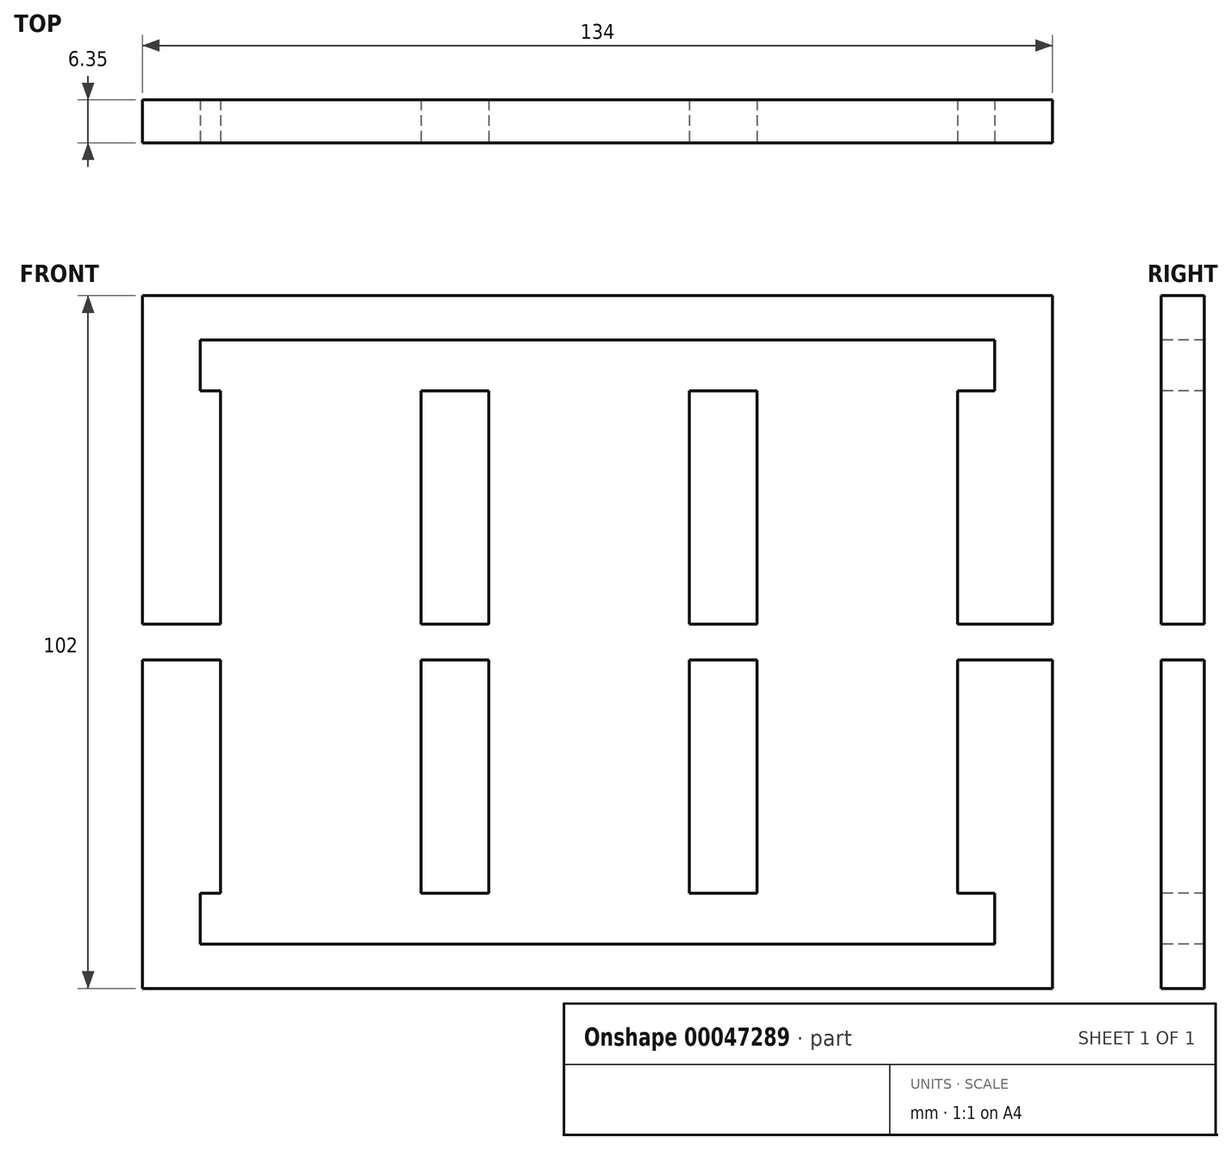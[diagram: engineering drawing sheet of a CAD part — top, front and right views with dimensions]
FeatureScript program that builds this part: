
annotation { "Feature Type Name" : "Feature", "Feature Type Description" : "" }
export const myFeature = defineFeature(function(context is Context, id is Id, definition is map)
    precondition{}
    {
        {
            var Q0;
            Q0=qCreatedBy(makeId("Front.planeOp"),FACE);
            var sketch = newSketch(context, id + "F0", { "sketchPlane" : qUnion([Q0])});
            skLineSegment(sketch, "E0.rect.bottom", {"start": v(67, -51) * mm, "end": v(-67, -51) * mm});
            skLineSegment(sketch, "E0.rect.top", {"start": v(67, 51) * mm, "end": v(-67, 51) * mm});
            skLineSegment(sketch, "E0.rect.left", {"start": v(67, -51) * mm, "end": v(67, 51) * mm});
            skLineSegment(sketch, "E0.rect.right", {"start": v(-67, -51) * mm, "end": v(-67, 51) * mm});
            skPoint(sketch, "E0.rect.middle", {"position": v(0, 0) * mm});
            skLineSegment(sketch, "E1", {"start": v(0, 51) * mm, "end": v(0, -51) * mm, "construction": true});
            skLineSegment(sketch, "E2", {"start": v(-67, 0) * mm, "end": v(67, 0) * mm, "construction": true});
            skSolve(sketch);
        }
        {
            var Q0;
            Q0=makeQuery(id+"F0.imprint","IMPRINT",FACE,{"disambiguationData":[TD([[makeQuery(id+"F0.imprint","IMPRINT",EDGE,{"derivedFrom":sQuery(id+"F0.wireOp",EDGE,"E0.rect.bottom")}),-1.0]])]});
            extrude(context, id + "F1", {"entities" : qUnion([Q0]), "depth" : 6.35 * mm});
        }
        {
            var Q0;
            Q0=makeQuery(id+"F1.opExtrude","CAP_FACE",FACE,{"disambiguationData":[OSD([sQuery(id+"F0.wireOp",EDGE,"E0.rect.bottom"),sQuery(id+"F0.wireOp",EDGE,"E0.rect.top"),sQuery(id+"F0.wireOp",EDGE,"E0.rect.left"),sQuery(id+"F0.wireOp",EDGE,"E0.rect.right")])],"isStart":false});
            var sketch = newSketch(context, id + "F2", { "sketchPlane" : qUnion([Q0])});
            skLineSegment(sketch, "E3.bottom", {"start": v(-16, 39.8) * mm, "end": v(13.5, 39.8) * mm});
            skLineSegment(sketch, "E3.top", {"start": v(-16, -39.8) * mm, "end": v(13.5, -39.8) * mm});
            skLineSegment(sketch, "E3.left", {"start": v(-16, 39.8) * mm, "end": v(-16, -39.8) * mm});
            skLineSegment(sketch, "E3.right", {"start": v(13.5, 39.8) * mm, "end": v(13.5, -39.8) * mm});
            skLineSegment(sketch, "E4.bottom", {"start": v(23.5, 39.8) * mm, "end": v(53, 39.8) * mm});
            skLineSegment(sketch, "E4.top", {"start": v(23.5, -39.8) * mm, "end": v(53, -39.8) * mm});
            skLineSegment(sketch, "E4.left", {"start": v(23.5, 39.8) * mm, "end": v(23.5, -39.8) * mm});
            skLineSegment(sketch, "E4.right", {"start": v(53, 39.8) * mm, "end": v(53, -39.8) * mm});
            skLineSegment(sketch, "E5.bottom", {"start": v(-55.5, 39.8) * mm, "end": v(-26, 39.8) * mm});
            skLineSegment(sketch, "E5.top", {"start": v(-55.5, -39.8) * mm, "end": v(-26, -39.8) * mm});
            skLineSegment(sketch, "E5.left", {"start": v(-55.5, 39.8) * mm, "end": v(-55.5, -39.8) * mm});
            skLineSegment(sketch, "E5.right", {"start": v(-26, 39.8) * mm, "end": v(-26, -39.8) * mm});
            skLineSegment(sketch, "E6", {"start": v(-67, 0) * mm, "end": v(-55.5, 0) * mm, "construction": true});
            skLineSegment(sketch, "E7", {"start": v(53, -16.02) * mm, "end": v(67, -16.02) * mm});
            skSolve(sketch);
        }
        {
            var Q0;
            Q0=qSketchRegion(id+"F2",true);
            extrude(context, id + "F3", {"entities" : qUnion([Q0]), "operationType" : NewBodyOperationType.REMOVE, "oppositeDirection" : true, "depth" : 12.7 * mm});
        }
        {
            var Q0;
            Q0=makeQuery(id+"F1.opExtrude","CAP_FACE",FACE,{"disambiguationData":[OSD([sQuery(id+"F0.wireOp",EDGE,"E0.rect.bottom"),sQuery(id+"F0.wireOp",EDGE,"E0.rect.top"),sQuery(id+"F0.wireOp",EDGE,"E0.rect.left"),sQuery(id+"F0.wireOp",EDGE,"E0.rect.right")])],"isStart":false});
            var sketch = newSketch(context, id + "F4", { "sketchPlane" : qUnion([Q0])});
            skLineSegment(sketch, "E8.bottom", {"start": v(-58.5, 44.5) * mm, "end": v(58.5, 44.5) * mm});
            skLineSegment(sketch, "E8.top", {"start": v(-58.5, 37) * mm, "end": v(58.5, 37) * mm});
            skLineSegment(sketch, "E8.left", {"start": v(-58.5, 44.5) * mm, "end": v(-58.5, 37) * mm});
            skLineSegment(sketch, "E8.right", {"start": v(58.5, 44.5) * mm, "end": v(58.5, 37) * mm});
            skPoint(sketch, "E9.rect.middle", {"position": v(0, 0) * mm});
            skLineSegment(sketch, "E10.rect.bottom", {"start": v(67, -2.63) * mm, "end": v(-67, -2.63) * mm});
            skLineSegment(sketch, "E10.rect.top", {"start": v(67, 2.62) * mm, "end": v(-67, 2.62) * mm});
            skLineSegment(sketch, "E10.rect.left", {"start": v(67, -2.63) * mm, "end": v(67, 2.62) * mm});
            skLineSegment(sketch, "E10.rect.right", {"start": v(-67, -2.63) * mm, "end": v(-67, 2.62) * mm});
            skPoint(sketch, "E11", {"position": v(-67, 0) * mm});
            skPoint(sketch, "E12", {"position": v(67, 0) * mm});
            skLineSegment(sketch, "E13", {"start": v(-67, 0) * mm, "end": v(67, 0) * mm, "construction": true});
            skLineSegment(sketch, "E14.MirrorCS", {"start": v(-58.5, -44.5) * mm, "end": v(-58.5, -37) * mm});
            skLineSegment(sketch, "E15.MirrorCS", {"start": v(-58.5, -44.5) * mm, "end": v(58.5, -44.5) * mm});
            skLineSegment(sketch, "E16.MirrorCS", {"start": v(58.5, -44.5) * mm, "end": v(58.5, -37) * mm});
            skLineSegment(sketch, "E17.MirrorCS", {"start": v(-58.5, -37) * mm, "end": v(58.5, -37) * mm});
            skLineSegment(sketch, "E18", {"start": v(-58.5, 37) * mm, "end": v(-67, 37) * mm});
            skLineSegment(sketch, "E19", {"start": v(58.5, 37) * mm, "end": v(67, 37) * mm});
            skSolve(sketch);
        }
        {
            var Q0;
            Q0=qSketchRegion(id+"F4",true);
            extrude(context, id + "F5", {"entities" : qUnion([Q0]), "operationType" : NewBodyOperationType.REMOVE, "oppositeDirection" : true, "depth" : 6.35 * mm});
        }
    });
